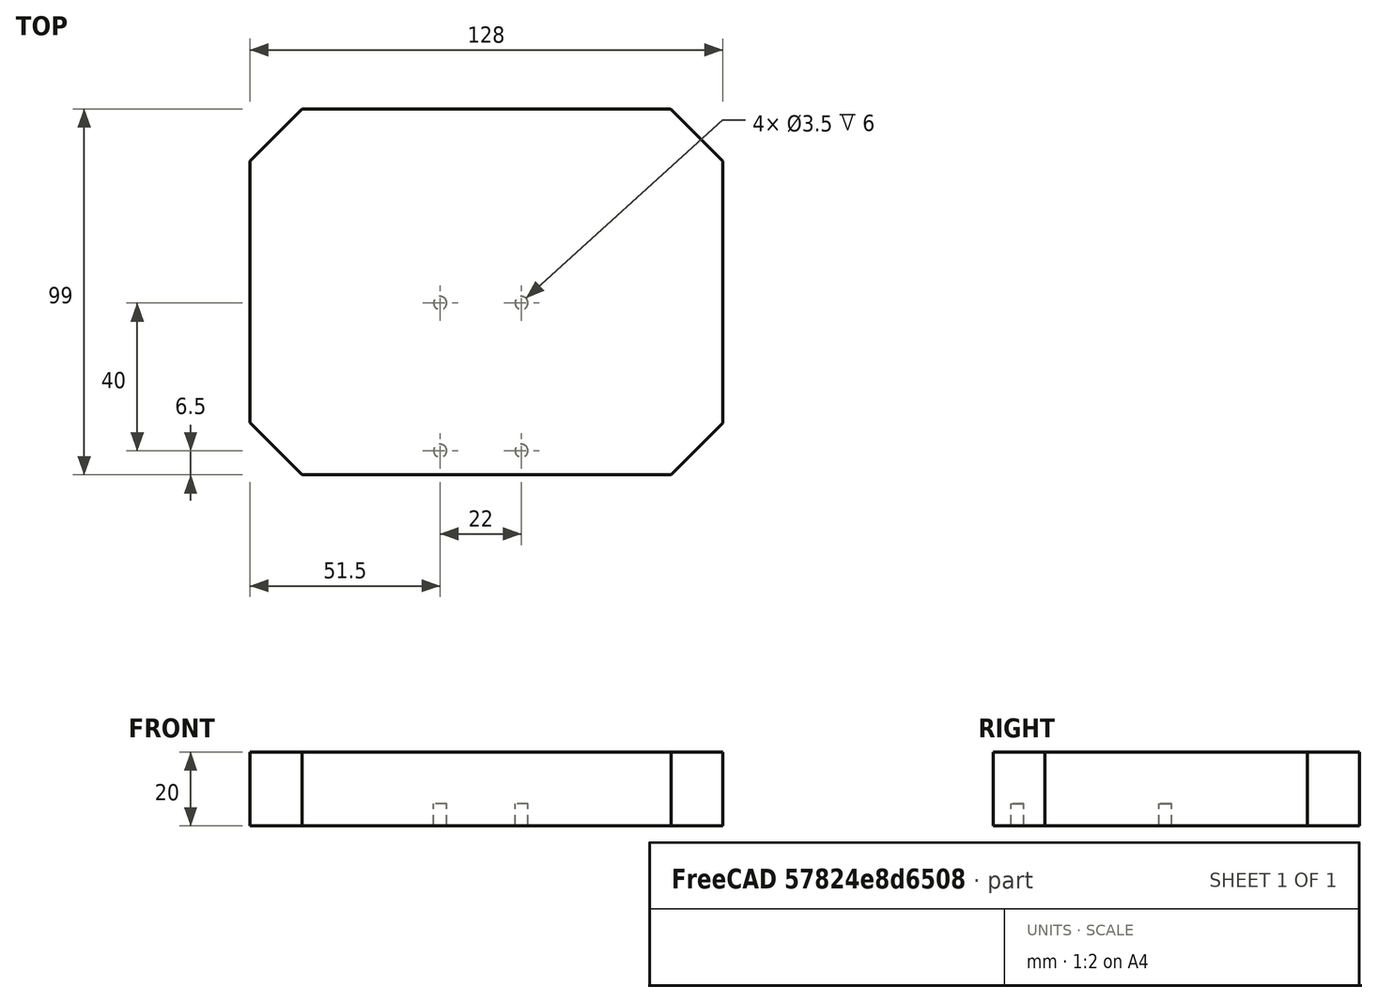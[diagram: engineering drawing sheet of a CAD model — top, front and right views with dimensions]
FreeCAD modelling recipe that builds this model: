
FCSTD DOCUMENT  (FreeCAD 0.15R4671 (Git))
Label: bloque metacrilato
License: All rights reserved
LicenseURL: http://en.wikipedia.org/wiki/All_rights_reserved
objects: Part::Box×5, Part::Cut×2, Part::MultiFuse×1, Part::Cylinder×1, Part::FeaturePython×1
note: 10 computed .brp shape members not serialized (recipe doc carries the construction recipe); baked Part::Feature solids carry a one-line shape summary decoded from their .brp

FEATURE [Part::Box] Box001  label="Superficie metacrilato"
  Height = 20
  Length = 128
  Placement = pos=(-14,-14.5,0) rot=(0,0,1;0rad)
  Width = 99
FEATURE [Part::Box] Box002  label="Cubo002"
  Height = 20
  Length = 20
  Placement = pos=(100,-14.5,0) rot=(0,0,-1;0.785398rad)
  Width = 20
FEATURE [Part::Box] Box  label="Cubo003"
  Height = 20
  Length = 20
  Placement = pos=(99.8,84.5,0) rot=(0,0,-1;0.785398rad)
  Width = 20
FEATURE [Part::Box] Box003  label="Cubo004"
  Height = 20
  Length = 20
  Placement = pos=(-14,-28.65,0) rot=(0,0,1;0.785398rad)
  Width = 20
FEATURE [Part::Box] Box004  label="Cubo005"
  Height = 20
  Length = 20
  Placement = pos=(-14,70.35,0) rot=(0,0,1;0.785398rad)
  Width = 20
FEATURE [Part::MultiFuse] Fusion
  Shapes = -> [Box,Box003,Box004,Box002]
FEATURE [Part::Cut] Cut
  Base = -> Box001
  Tool = -> Fusion
FEATURE [Part::Cylinder] Cylinder  label="Cilindro"
  Angle = 360
  Height = 6
  Radius = 1.75
FEATURE [Part::FeaturePython] Array  # Draft array (typed FeaturePython)
  Angle = 360
  ArrayType = 0
  Axis = (0,0,1)
  Base = -> Cylinder
  Center = (0,0,0)
  Fuse = false
  IntervalAxis = (0,0,0)
  IntervalX = (22,0,0)
  IntervalY = (0,40,0)
  IntervalZ = (0,0,0)
  NumberPolar = 1
  NumberX = 2
  NumberY = 2
  NumberZ = 1
  Placement = pos=(37.5,-8,0) rot=(0,0,1;0rad)
FEATURE [Part::Cut] Cut001
  Base = -> Cut
  Tool = -> Array
